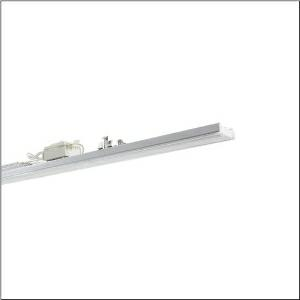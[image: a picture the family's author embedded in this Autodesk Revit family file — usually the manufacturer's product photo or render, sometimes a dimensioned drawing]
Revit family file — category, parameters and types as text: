
# Revit family: licross_r__11_recessed_mo_51tl197n485g_1cc2
name_source: partatom
category: Lighting Fixtures
units: mm (PartAtom-declared; Revit-internal decimal feet)

## family parameters
Cut with Voids When Loaded = No
Host = Face
Light Source = No
Part Type = Normal
Room Calculation Point = No
Round Connector Dimension = Use Diameter
Shared = No

## types (1)
- Licross® 11 Recessed MO (1 x LED, 8580 lm, 48.5 W, 4000K)
    Apparent Load = 49 VA
    CIE Flux Codes = 55 90 98 100 100
    Color Rendering = 80
    Color Temperature = 4000K
    Default Elevation = 1800 mm
    Description = Licross® 11 Recessed MO, luminaire insert, of sheet steel, coil coated, white, length: 1.500mm, width: 66mm, height: 67mm, LED rated luminous flux: 8.580lm, light colour: 840, control gear: ON/OFF, with plug, 3-pole, with phase selection, mains connection: 220..240V, AC, 50/60Hz, rated input power: 49W, halogen-free wiring, primary light control with lens, of plastic, primary optical cover: cover, of PMMA, light emission: direct distribution, primary light characteristic: double asymmetric, protection rating (complete): IP40, insulation class (complete): insulation class I (protective earthing), certification: CE, ENEC, VDE, UKCA, protection symbol: D if used in an environment without relevant dust loads with corresponding accessories, impact resistance: IK06, permissible ambient temperature for indoor applications: -35..+35°C, corresponds to IFS (International Featured Standards) requirements for safety and quality in the food industry, reducing of maximum allowable ambient temperature of 5°C with ceiling mounting, packaging unit: 1 piece
    Height = 58 mm
    Lamp = 1 x LED
    Lamp Light Flux = 8580 lm
    Lamp Power = 48.5 W
    Lamp count = 1
    Length = 1500 mm
    Luminous efficacy = 177 lm/W
    Manufacturer = Siteco
    ModVariant = No
    Model = 51TL197N485G
    Mounting Place = Ceiling
    Mounting Type = Pendant
    Number of Poles = 1
    OnlyDefault = Yes
    Power Factor = 1
    Product Name = Licross® 11 Recessed MO
    Product group = luminaire insert
    ProductGroupID = 902
    Protection Class = Protection class I
    Protection Degree = IP 40
    RLX_Detail_Level = 1
    RLX_Emergency_Light_Flux = 0 lm
    RLX_Emergency_Type = 0
    RLX_Emergency_Type_DB = No
    RlxData = <blob elided: 20781 chars, md5=51da89d5>
    Socket = socket
    Standby Power = 0 W
    System Light Flux = 8580 lm
    System Power = 49 W
    Type Comments = Product without accessories
    Type Image = l_1296930.jpg
    URL = http://relux.com
    VarID = ---
    Voltage = 0 V
    Weight = 0.00 kg
    Width = 66 mm

## geometry (parser evidence)
native form markers: Blend x4, Sweep x9
no freeform markers — native parametric forms only
